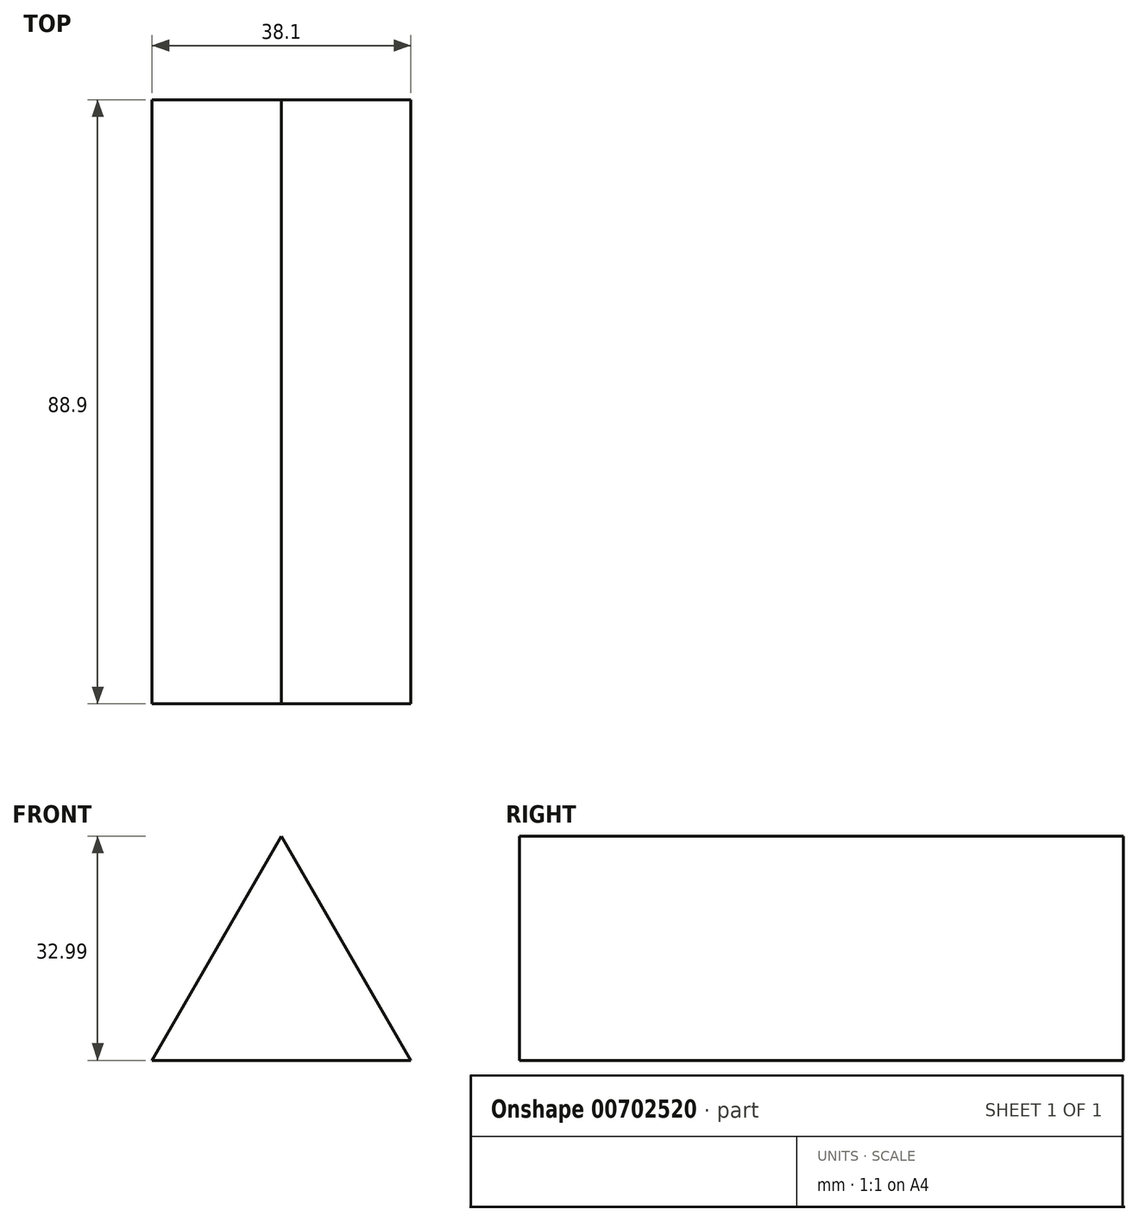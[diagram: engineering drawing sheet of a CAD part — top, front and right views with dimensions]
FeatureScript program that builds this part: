
annotation { "Feature Type Name" : "Feature", "Feature Type Description" : "" }
export const myFeature = defineFeature(function(context is Context, id is Id, definition is map)
    precondition{}
    {
        {
            var Q0;
            Q0=qCreatedBy(makeId("Front.planeOp"),FACE);
            var sketch = newSketch(context, id + "F0", { "sketchPlane" : qUnion([Q0])});
            skLineSegment(sketch, "E0", {"start": v(-19.05, -16.97) * mm, "end": v(0, 16.02) * mm});
            skLineSegment(sketch, "E1", {"start": v(0, 16.02) * mm, "end": v(19.05, -16.97) * mm});
            skLineSegment(sketch, "E2", {"start": v(19.05, -16.97) * mm, "end": v(-19.05, -16.97) * mm});
            skSolve(sketch);
        }
        {
            var Q0;
            Q0 = qSketchRegion(id + "F0", true);
            extrude(context, id + "F1", {"entities" : qUnion([Q0]), "depth" : 88.9 * mm, "offsetDistance" : 25.4 * mm});
        }
    });
